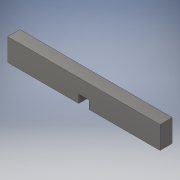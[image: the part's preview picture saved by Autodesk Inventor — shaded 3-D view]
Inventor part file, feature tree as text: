
AUTODESK INVENTOR PART (.ipt)
format: ipt  version: 2017 SP1 (Build 210196100, 196)  size: 98,816 bytes
history: native  units: in
note: dims shown in document units (in); Inventor stores cm internally (conversion verified against a paired STEP export)
features: extrude x1, sketch x1
ambient origin geometry x8: Origin, YZ Plane, XZ Plane, XY Plane, X Axis, Y Axis, Z Axis, Center Point
bodies: Solid1 (feature_tree)
feature tree (2):
  extrude  "Extrusion1"  Depth=0.125in
  sketch  "Sketch1"  dims[d0=0.1562in d1=0.125in d2=2.3125in d3=0.3405in d4=0.1855in d5=0.0in]
